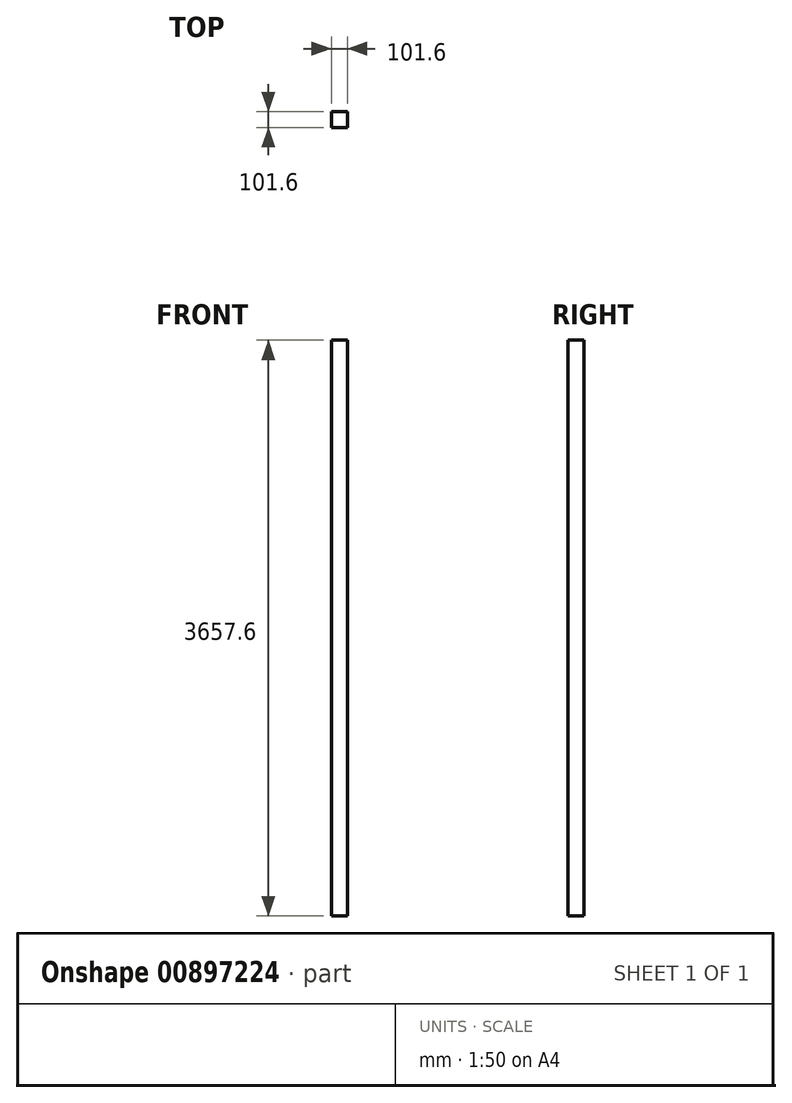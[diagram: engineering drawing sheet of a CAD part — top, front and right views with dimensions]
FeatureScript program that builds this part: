
annotation { "Feature Type Name" : "Feature", "Feature Type Description" : "" }
export const myFeature = defineFeature(function(context is Context, id is Id, definition is map)
    precondition{}
    {
        {
            var Q0;
            Q0=qCreatedBy(makeId("Top.planeOp"),FACE);
            var sketch = newSketch(context, id + "F0", { "sketchPlane" : qUnion([Q0])});
            skLineSegment(sketch, "E0.bottom", {"start": v(0, 0) * mm, "end": v(101.6, 0) * mm});
            skLineSegment(sketch, "E0.top", {"start": v(0, 101.6) * mm, "end": v(101.6, 101.6) * mm});
            skLineSegment(sketch, "E0.left", {"start": v(0, 0) * mm, "end": v(0, 101.6) * mm});
            skLineSegment(sketch, "E0.right", {"start": v(101.6, 0) * mm, "end": v(101.6, 101.6) * mm});
            skSolve(sketch);
        }
        {
            var Q0;
            Q0 = qSketchRegion(id + "F0", true);
            extrude(context, id + "F1", {"entities" : qUnion([Q0]), "depth" : 3657.6 * mm, "offsetDistance" : 25.4 * mm});
        }
    });
